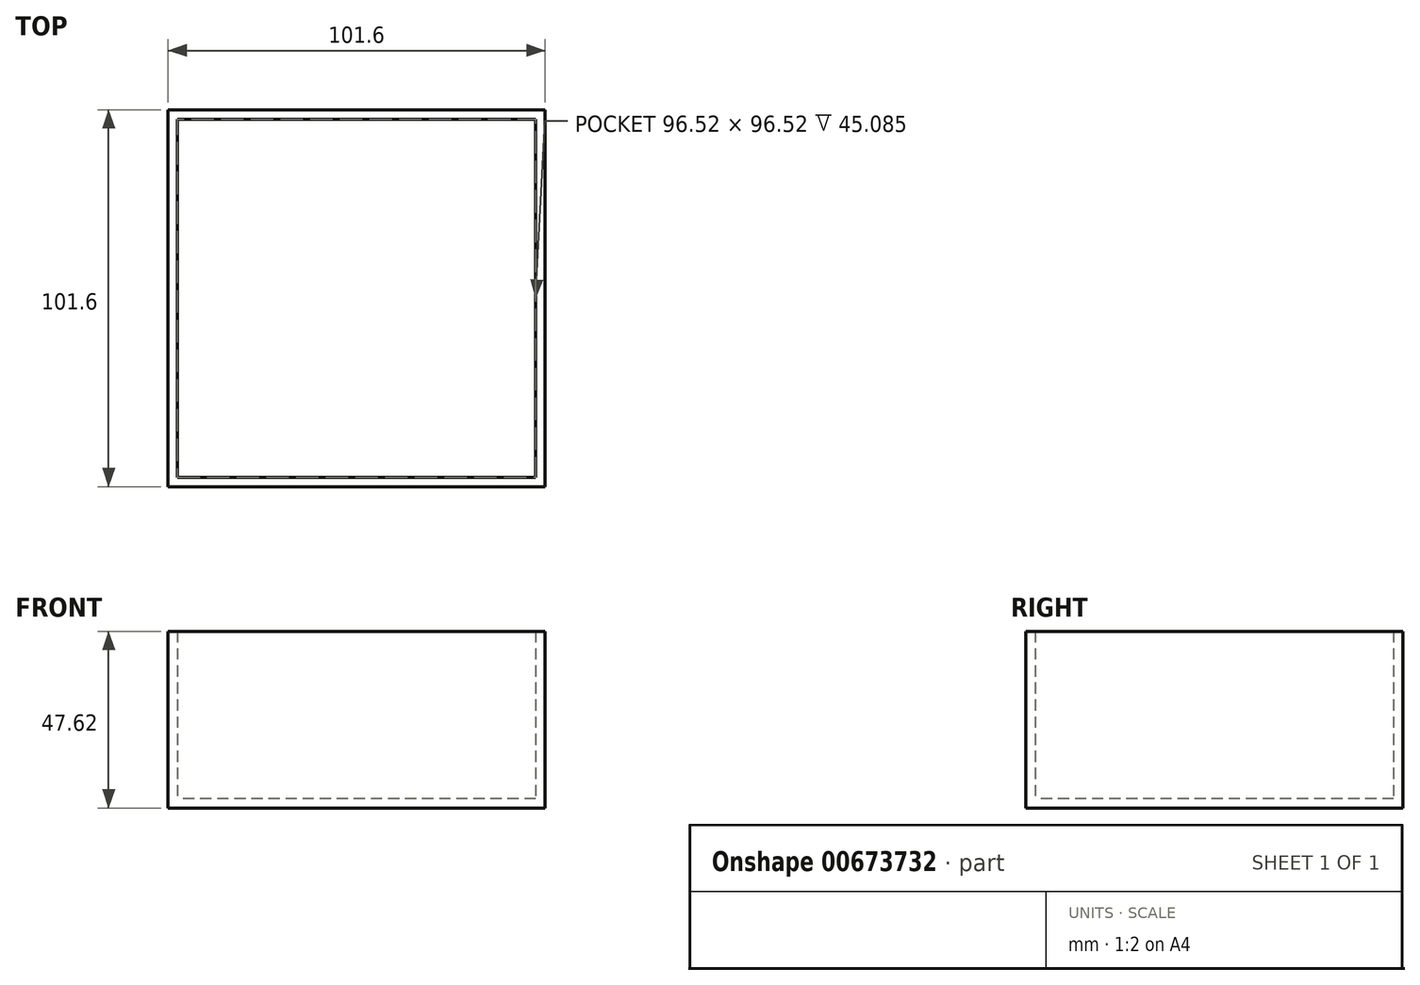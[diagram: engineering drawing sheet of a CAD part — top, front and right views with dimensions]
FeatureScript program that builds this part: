
annotation { "Feature Type Name" : "Feature", "Feature Type Description" : "" }
export const myFeature = defineFeature(function(context is Context, id is Id, definition is map)
    precondition{}
    {
        {
            var Q0;
            Q0=qCreatedBy(makeId("Top.planeOp"),FACE);
            var sketch = newSketch(context, id + "F0", { "sketchPlane" : qUnion([Q0])});
            skLineSegment(sketch, "E0.bottom", {"start": v(50.8, 50.8) * mm, "end": v(-50.8, 50.8) * mm});
            skLineSegment(sketch, "E0.top", {"start": v(50.8, -50.8) * mm, "end": v(-50.8, -50.8) * mm});
            skLineSegment(sketch, "E0.left", {"start": v(50.8, 50.8) * mm, "end": v(50.8, -50.8) * mm});
            skLineSegment(sketch, "E0.right", {"start": v(-50.8, 50.8) * mm, "end": v(-50.8, -50.8) * mm});
            skPoint(sketch, "E0.middle", {"position": v(0, 0) * mm});
            skLineSegment(sketch, "E1.bottom", {"start": v(48.26, 48.26) * mm, "end": v(-48.26, 48.26) * mm});
            skLineSegment(sketch, "E1.top", {"start": v(48.26, -48.26) * mm, "end": v(-48.26, -48.26) * mm});
            skLineSegment(sketch, "E1.left", {"start": v(48.26, 48.26) * mm, "end": v(48.26, -48.26) * mm});
            skLineSegment(sketch, "E1.right", {"start": v(-48.26, 48.26) * mm, "end": v(-48.26, -48.26) * mm});
            skSolve(sketch);
        }
        {
            var Q0;
            Q0=makeQuery(id+"F0.imprint","IMPRINT",FACE,{"disambiguationData":[TD([[makeQuery(id+"F0.imprint","IMPRINT",EDGE,{"derivedFrom":sQuery(id+"F0.wireOp",EDGE,"E0.bottom")}),1.0]])]});
            extrude(context, id + "F1", {"entities" : qUnion([Q0]), "depth" : 47.62 * mm, "offsetDistance" : 25.4 * mm});
        }
        {
            var Q0;
            Q0 = qSketchRegion(id + "F0", true);
            var Q1;
            Q1=makeQuery(id+"F0.imprint","IMPRINT",FACE,{"disambiguationData":[TD([[makeQuery(id+"F0.imprint","IMPRINT",EDGE,{"derivedFrom":sQuery(id+"F0.wireOp",EDGE,"E1.bottom")}),1.0]])]});
            extrude(context, id + "F2", {"entities" : qUnion([Q0, Q1]), "operationType" : NewBodyOperationType.ADD, "depth" : 2.54 * mm, "offsetDistance" : 25.4 * mm});
        }
    });
